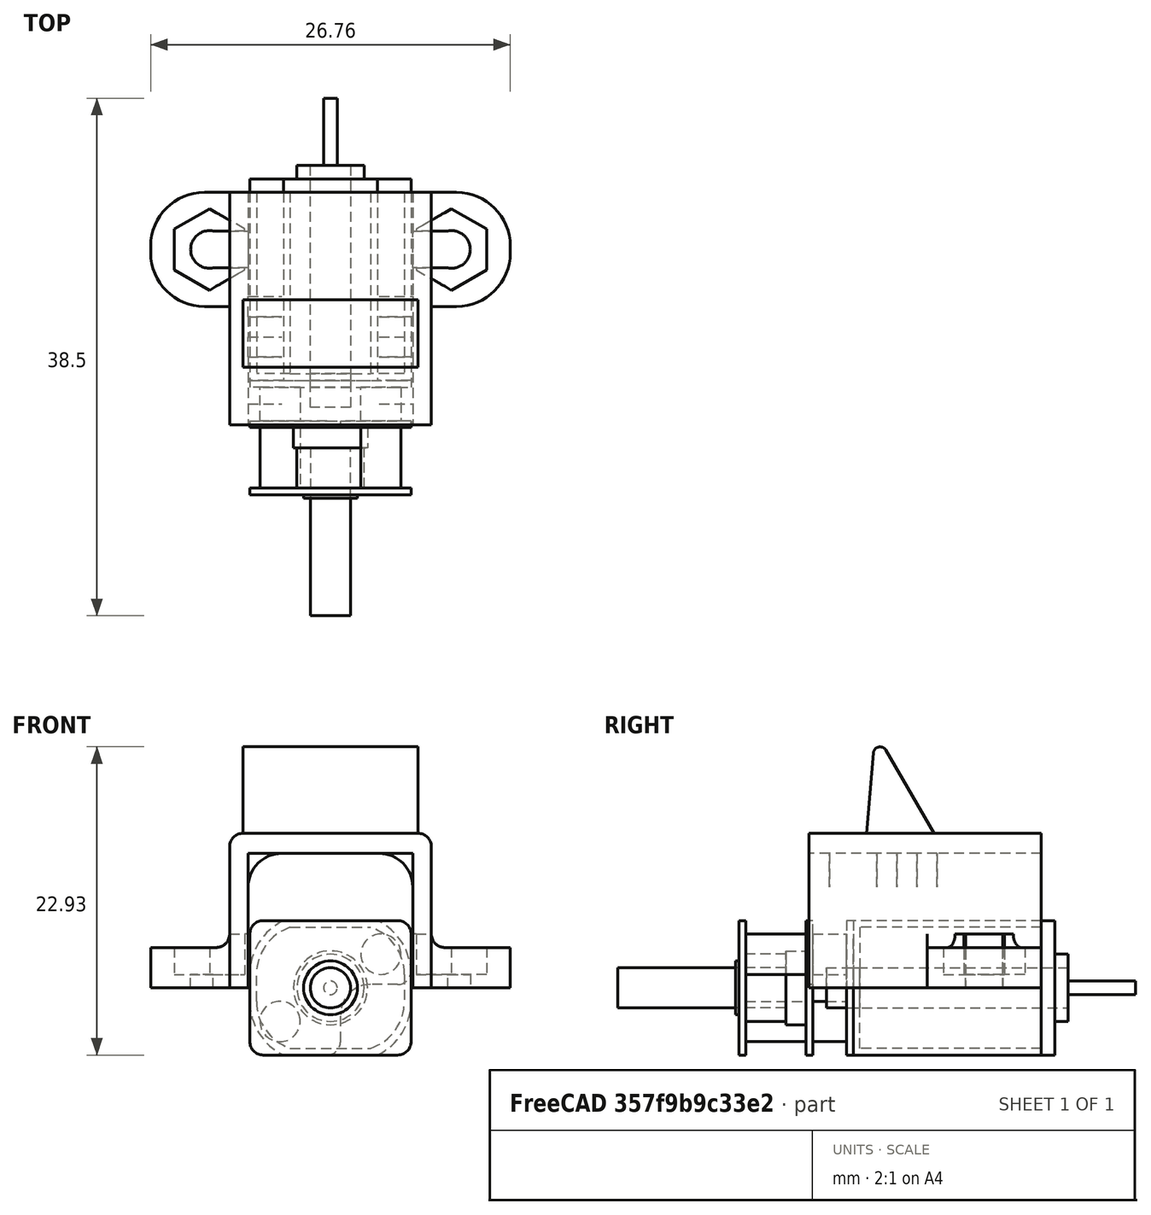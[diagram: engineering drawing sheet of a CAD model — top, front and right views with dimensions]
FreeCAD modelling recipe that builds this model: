
FCSTD DOCUMENT  (FreeCAD 0.19R24276 (Git))
Label: PB3D_MotorAndBracket
License: All rights reserved
LicenseURL: http://en.wikipedia.org/wiki/All_rights_reserved
objects: Sketcher::SketchObject×26, PartDesign::Pad×15, PartDesign::Pocket×11, PartDesign::Body×7, PartDesign::Plane×6, App::Part×2, PartDesign::Fillet×1, PartDesign::ShapeBinder×1, Mesh::Feature×1
note: 94 computed .brp shape members not serialized (recipe doc carries the construction recipe); baked Part::Feature solids carry a one-line shape summary decoded from their .brp

FEATURE [Sketcher::SketchObject] Sketch
  FullyConstrained = true
  MapMode = 5
  Placement = pos=(0,0,0) rot=(1,0,0;1.5708rad)
  Support = -> [XZ_Plane]
  sketch-geometry (12):
    g0: LineSegment StartX=-3.5 StartY=5 StartZ=0 EndX=3.5 EndY=5 EndZ=0
    g1: LineSegment StartX=-3.5 StartY=-5 StartZ=0 EndX=3.5 EndY=-5 EndZ=0
    g2: LineSegment StartX=6 StartY=1 StartZ=0 EndX=6 EndY=-1 EndZ=0
    g3: LineSegment StartX=-6 StartY=1 StartZ=0 EndX=-6 EndY=-1 EndZ=0
    g4: LineSegment StartX=0 StartY=0 StartZ=0 EndX=-6 EndY=0 EndZ=0
    g5: LineSegment StartX=0 StartY=0 StartZ=0 EndX=6 EndY=0 EndZ=0
    g6: LineSegment StartX=0 StartY=0 StartZ=0 EndX=0 EndY=5 EndZ=0
    g7: LineSegment StartX=0 StartY=0 StartZ=0 EndX=0 EndY=-5 EndZ=0
    g8: ArcOfCircle CenterX=-1.55001 CenterY=1.00001 CenterZ=0 NormalX=0 NormalY=0 NormalZ=1 AngleXU=0 Radius=4.44999 StartAngle=2.02439 EndAngle=3.14159
    g9: ArcOfCircle CenterX=1.55001 CenterY=1.00001 CenterZ=0 NormalX=0 NormalY=0 NormalZ=1 AngleXU=0 Radius=4.44999 StartAngle=6.28318 EndAngle=7.40039
    g10: ArcOfCircle CenterX=-1.55001 CenterY=-1.00001 CenterZ=0 NormalX=0 NormalY=0 NormalZ=1 AngleXU=0 Radius=4.44999 StartAngle=3.14159 EndAngle=4.25879
    g11: ArcOfCircle CenterX=1.55001 CenterY=-1.00001 CenterZ=0 NormalX=0 NormalY=0 NormalZ=1 AngleXU=0 Radius=4.44999 StartAngle=5.16598 EndAngle=6.28319
  constraints (36):
    c: Horizontal(g0)
    c: Horizontal(g1)
    c: Vertical(g2)
    c: Vertical(g3)
    c: Equal(g0,g1)
    c: Equal(g3,g2)
    c: Coincident(g4,g-1)
    c: Coincident(g5,g-1)
    c: Horizontal(g5)
    c: Coincident(g6,g-1)
    c: Coincident(g7,g-1)
    c: Vertical(g7)
    c: Vertical(g6)
    c: Horizontal(g4)
    c: Equal(g4,g5)
    c: Equal(g7,g6)
    c: Symmetric(g3,g3,g4)
    c: Symmetric(g2,g2,g5)
    c: Symmetric(g1,g1,g7)
    c: Symmetric(g0,g0,g6)
    c: Coincident(g8,g3)
    c: Coincident(g8,g0)
    c: Tangent(g8,g3)
    c: Coincident(g9,g0)
    c: Coincident(g9,g2)
    c: Coincident(g10,g3)
    c: Coincident(g10,g1)
    c: Coincident(g11,g1)
    c: Coincident(g11,g2)
    c: Tangent(g3,g10)
    c: Tangent(g9,g2)
    c: Tangent(g11,g2)
    c: DistanceY(g1,g0) = 10
    c: Distance(g2) = 2
    c: DistanceX(g3,g2) = 12
    c: DistanceX(g0,g0) = 7
FEATURE [PartDesign::Pad] Pad
  Direction = (1,1,1)
  Length = 14
  Length2 = 100
  Placement = pos=(0,0,0) rot=(1,0,0;1.5708rad)
  Profile = -> Sketch
  Type = 0
FEATURE [Sketcher::SketchObject] Sketch001
  FullyConstrained = true
  MapMode = 5
  Placement = pos=(0,0,0) rot=(1,0,0;1.5708rad)
  Support = -> [XZ_Plane]
  sketch-geometry (12):
    g0: LineSegment StartX=-3 StartY=4.5 StartZ=0 EndX=3 EndY=4.5 EndZ=0
    g1: LineSegment StartX=5.5 StartY=1 StartZ=0 EndX=5.5 EndY=-1 EndZ=0
    g2: LineSegment StartX=-3 StartY=-4.5 StartZ=0 EndX=3 EndY=-4.5 EndZ=0
    g3: LineSegment StartX=-5.5 StartY=-1 StartZ=0 EndX=-5.5 EndY=1 EndZ=0
    g4: LineSegment StartX=0 StartY=0 StartZ=0 EndX=0 EndY=4.5 EndZ=0
    g5: LineSegment StartX=0 StartY=0 StartZ=0 EndX=5.5 EndY=0 EndZ=0
    g6: LineSegment StartX=0 StartY=0 StartZ=0 EndX=0 EndY=-4.5 EndZ=0
    g7: LineSegment StartX=0 StartY=0 StartZ=0 EndX=-5.5 EndY=0 EndZ=0
    g8: ArcOfCircle CenterX=-1.79999 CenterY=0.999993 CenterZ=0 NormalX=0 NormalY=0 NormalZ=1 AngleXU=0 Radius=3.70001 StartAngle=1.9011 EndAngle=3.14159
    g9: ArcOfCircle CenterX=1.79999 CenterY=0.999993 CenterZ=0 NormalX=0 NormalY=0 NormalZ=1 AngleXU=0 Radius=3.70001 StartAngle=1.80818e-06 EndAngle=1.2405
    g10: ArcOfCircle CenterX=1.79999 CenterY=-0.999993 CenterZ=0 NormalX=0 NormalY=0 NormalZ=1 AngleXU=0 Radius=3.70001 StartAngle=5.04269 EndAngle=6.28318
    g11: ArcOfCircle CenterX=-1.79999 CenterY=-0.999993 CenterZ=0 NormalX=0 NormalY=0 NormalZ=1 AngleXU=0 Radius=3.70001 StartAngle=3.14159 EndAngle=4.38209
  constraints (36):
    c: Vertical(g3)
    c: Vertical(g1)
    c: Horizontal(g0)
    c: Horizontal(g2)
    c: Coincident(g4,g-1)
    c: Coincident(g5,g-1)
    c: Coincident(g6,g-1)
    c: Coincident(g7,g-1)
    c: Horizontal(g7)
    c: Horizontal(g5)
    c: Vertical(g4)
    c: Vertical(g6)
    c: Equal(g3,g1)
    c: Equal(g0,g2)
    c: Equal(g6,g4)
    c: Equal(g5,g7)
    c: Symmetric(g0,g0,g4)
    c: Symmetric(g1,g1,g5)
    c: Symmetric(g3,g3,g7)
    c: Symmetric(g2,g2,g6)
    c: Coincident(g8,g3)
    c: Coincident(g8,g0)
    c: Coincident(g9,g0)
    c: Coincident(g9,g1)
    c: Coincident(g10,g1)
    c: Coincident(g10,g2)
    c: Coincident(g11,g3)
    c: Coincident(g11,g2)
    c: Tangent(g8,g3)
    c: Tangent(g11,g3)
    c: Tangent(g10,g1)
    c: Tangent(g9,g1)
    c: Distance(g0) = 6
    c: Distance(g1) = 2
    c: DistanceX(g3,g1) = 11
    c: DistanceY(g2,g0) = 9
FEATURE [PartDesign::Pocket] Pocket
  BaseFeature = -> Pad
  Length = 13.5
  Length2 = 100
  Placement = pos=(0,0,0) rot=(1,0,0;1.5708rad)
  Profile = -> Sketch001
  Reversed = true
  Type = 0
FEATURE [Sketcher::SketchObject] Sketch002
  FullyConstrained = true
  MapMode = 5
  Placement = pos=(0,0,0) rot=(1,0,0;1.5708rad)
  Support = -> [XZ_Plane]
  sketch-geometry (1):
    g0: Circle CenterX=0 CenterY=0 CenterZ=0 NormalX=0 NormalY=0 NormalZ=1 AngleXU=0 Radius=1.5
  constraints (2):
    c: Coincident(g0,g-1)
    c: Diameter(g0) = 3
FEATURE [PartDesign::Pocket] Pocket001
  BaseFeature = -> Pocket
  Length = 5
  Length2 = 100
  Placement = pos=(0,0,0) rot=(1,0,0;1.5708rad)
  Profile = -> Sketch002
  Reversed = true
  Type = 1
FEATURE [PartDesign::Body] Body  label="MotorShell"
  Group = -> [Sketch,Pad,Sketch001,Pocket,Sketch002,Pocket001]
  Origin = -> Origin
  Tip = -> Pocket001
FEATURE [Sketcher::SketchObject] Sketch003
  FullyConstrained = true
  MapMode = 5
  Placement = pos=(0,0,0) rot=(1,0,0;1.5708rad)
  Support = -> [XZ_Plane002]
  sketch-geometry (12):
    g0: LineSegment StartX=-3.5 StartY=5 StartZ=0 EndX=3.5 EndY=5 EndZ=0
    g1: LineSegment StartX=6 StartY=1 StartZ=0 EndX=6 EndY=-1 EndZ=0
    g2: LineSegment StartX=3.5 StartY=-5 StartZ=0 EndX=-3.5 EndY=-5 EndZ=0
    g3: LineSegment StartX=-6 StartY=-1 StartZ=0 EndX=-6 EndY=1 EndZ=0
    g4: LineSegment StartX=0 StartY=0 StartZ=0 EndX=-6 EndY=0 EndZ=0
    g5: LineSegment StartX=0 StartY=0 StartZ=0 EndX=6 EndY=0 EndZ=0
    g6: LineSegment StartX=0 StartY=0 StartZ=0 EndX=0 EndY=5 EndZ=0
    g7: LineSegment StartX=0 StartY=0 StartZ=0 EndX=0 EndY=-5 EndZ=0
    g8: ArcOfCircle CenterX=-1.55 CenterY=1 CenterZ=0 NormalX=0 NormalY=0 NormalZ=1 AngleXU=0 Radius=4.45 StartAngle=2.02439 EndAngle=3.14159
    g9: ArcOfCircle CenterX=1.55 CenterY=1 CenterZ=0 NormalX=0 NormalY=0 NormalZ=1 AngleXU=0 Radius=4.45 StartAngle=6.28319 EndAngle=7.40038
    g10: ArcOfCircle CenterX=1.55 CenterY=-1 CenterZ=0 NormalX=0 NormalY=0 NormalZ=1 AngleXU=0 Radius=4.45 StartAngle=5.16599 EndAngle=6.28319
    g11: ArcOfCircle CenterX=-1.55 CenterY=-1 CenterZ=0 NormalX=0 NormalY=0 NormalZ=1 AngleXU=0 Radius=4.45 StartAngle=3.14159 EndAngle=4.25879
  constraints (36):
    c: Coincident(g4,g-1)
    c: PointOnObject(g4,g-1)
    c: Coincident(g5,g-1)
    c: PointOnObject(g5,g-1)
    c: Coincident(g6,g-1)
    c: PointOnObject(g6,g-2)
    c: Coincident(g7,g-1)
    c: PointOnObject(g7,g-2)
    c: Equal(g4,g5)
    c: Equal(g7,g6)
    c: Equal(g0,g2)
    c: Equal(g1,g3)
    c: Vertical(g3)
    c: Vertical(g1)
    c: Horizontal(g0)
    c: Horizontal(g2)
    c: Symmetric(g3,g3,g4)
    c: Symmetric(g1,g1,g5)
    c: Symmetric(g0,g0,g6)
    c: Symmetric(g2,g2,g7)
    c: Coincident(g8,g3)
    c: Coincident(g8,g0)
    c: Coincident(g9,g0)
    c: Coincident(g9,g1)
    c: Coincident(g10,g1)
    c: Coincident(g10,g2)
    c: Coincident(g11,g2)
    c: Coincident(g11,g3)
    c: Tangent(g8,g3)
    c: Tangent(g3,g11)
    c: Tangent(g10,g1)
    c: Tangent(g1,g9)
    c: Distance(g1) = 2
    c: Distance(g0) = 7
    c: DistanceX(g3,g1) = 12
    c: DistanceY(g2,g0) = 10
FEATURE [PartDesign::Pad] Pad001
  Direction = (1,1,1)
  Length = 1
  Length2 = 100
  Placement = pos=(0,0,0) rot=(1,0,0;1.5708rad)
  Profile = -> Sketch003
  Reversed = true
  Type = 0
FEATURE [Sketcher::SketchObject] Sketch004
  FullyConstrained = true
  MapMode = 5
  Placement = pos=(0,1,-4e-16) rot=(-1,0,0;1.5708rad)
  Support = -> [Pad001]
  sketch-geometry (1):
    g0: Circle CenterX=0 CenterY=0 CenterZ=0 NormalX=0 NormalY=0 NormalZ=1 AngleXU=0 Radius=2.5
  constraints (2):
    c: Coincident(g0,g-1)
    c: Diameter(g0) = 5
FEATURE [PartDesign::Pad] Pad002
  BaseFeature = -> Pad001
  Direction = (1,1,1)
  Length = 1
  Length2 = 100
  Placement = pos=(0,0,0) rot=(1,0,0;1.5708rad)
  Profile = -> Sketch004
  Type = 0
FEATURE [Sketcher::SketchObject] Sketch005
  FullyConstrained = true
  MapMode = 5
  Placement = pos=(0,2,-1.8e-15) rot=(-1,0,0;1.5708rad)
  Support = -> [Pad002]
  sketch-geometry (1):
    g0: Circle CenterX=0 CenterY=0 CenterZ=0 NormalX=0 NormalY=0 NormalZ=1 AngleXU=0 Radius=1.5
  constraints (2):
    c: Coincident(g0,g-1)
    c: Diameter(g0) = 3
FEATURE [PartDesign::Pocket] Pocket002
  BaseFeature = -> Pad002
  Length = 5
  Length2 = 100
  Placement = pos=(0,0,0) rot=(1,0,0;1.5708rad)
  Profile = -> Sketch005
  Type = 1
FEATURE [PartDesign::Body] Body001  label="BackPlate"
  Group = -> [Sketch003,Pad001,Sketch004,Pad002,Sketch005,Pocket002]
  Origin = -> Origin002
  Tip = -> Pocket002
FEATURE [PartDesign::Plane] DatumPlane
  AttachmentOffset = pos=(0,0,14) rot=(0,0,1;0rad)
  Length = 60
  MapMode = 2
  Placement = pos=(0,-14,-3.1e-15) rot=(1,0,0;1.5708rad)
  ResizeMode = 0
  Support = -> [XZ_Plane003]
  Width = 60
FEATURE [Sketcher::SketchObject] Sketch006
  FullyConstrained = true
  MapMode = 5
  Placement = pos=(0,-14,-3.1e-15) rot=(1,0,0;1.5708rad)
  Support = -> [DatumPlane]
  sketch-geometry (6):
    g0: LineSegment StartX=-6 StartY=5 StartZ=0 EndX=6 EndY=5 EndZ=0
    g1: LineSegment StartX=6 StartY=5 StartZ=0 EndX=6 EndY=-5 EndZ=0
    g2: LineSegment StartX=6 StartY=-5 StartZ=0 EndX=-6 EndY=-5 EndZ=0
    g3: LineSegment StartX=-6 StartY=-5 StartZ=0 EndX=-6 EndY=5 EndZ=0
    g4: LineSegment StartX=0 StartY=0 StartZ=0 EndX=0 EndY=5 EndZ=0
    g5: LineSegment StartX=0 StartY=0 StartZ=0 EndX=6 EndY=-2e-16 EndZ=0
  constraints (16):
    c: Coincident(g0,g1)
    c: Coincident(g1,g2)
    c: Coincident(g2,g3)
    c: Coincident(g3,g0)
    c: Horizontal(g0)
    c: Horizontal(g2)
    c: Vertical(g1)
    c: Vertical(g3)
    c: Coincident(g4,g-1)
    c: PointOnObject(g4,g-2)
    c: Coincident(g5,g-1)
    c: PointOnObject(g5,g-1)
    c: Symmetric(g0,g0,g4)
    c: Symmetric(g0,g1,g5)
    c: Distance(g0) = 12
    c: Distance(g1) = 10
FEATURE [PartDesign::Pad] Pad003
  Direction = (1,1,1)
  Length = 0.5
  Length2 = 100
  Placement = pos=(0,-14,3e-15) rot=(1,0,0;1.5708rad)
  Profile = -> Sketch006
  Type = 0
FEATURE [Sketcher::SketchObject] Sketch007
  FullyConstrained = true
  MapMode = 5
  Placement = pos=(0,-14.5,3.3e-15) rot=(1,0,0;1.5708rad)
  Support = -> [Pad003]
  sketch-geometry (8):
    g0: Circle CenterX=3.75 CenterY=2.5 CenterZ=0 NormalX=0 NormalY=0 NormalZ=1 AngleXU=0 Radius=1.5
    g1: Circle CenterX=-3.75 CenterY=-2.5 CenterZ=0 NormalX=0 NormalY=0 NormalZ=1 AngleXU=0 Radius=1.5
    g2: LineSegment StartX=-3.75 StartY=2.5 StartZ=0 EndX=3.75 EndY=2.5 EndZ=0
    g3: LineSegment StartX=3.75 StartY=2.5 StartZ=0 EndX=3.75 EndY=-2.5 EndZ=0
    g4: LineSegment StartX=3.75 StartY=-2.5 StartZ=0 EndX=-3.75 EndY=-2.5 EndZ=0
    g5: LineSegment StartX=-3.75 StartY=-2.5 StartZ=0 EndX=-3.75 EndY=2.5 EndZ=0
    g6: LineSegment StartX=0 StartY=0 StartZ=0 EndX=0 EndY=2.5 EndZ=0
    g7: LineSegment StartX=0 StartY=0 StartZ=0 EndX=3.75 EndY=0 EndZ=0
  constraints (20):
    c: Equal(g0,g1)
    c: Diameter(g0) = 3
    c: Coincident(g2,g3)
    c: Coincident(g3,g4)
    c: Coincident(g4,g5)
    c: Coincident(g5,g2)
    c: Horizontal(g2)
    c: Horizontal(g4)
    c: Vertical(g3)
    c: Vertical(g5)
    c: Coincident(g6,g-1)
    c: Coincident(g7,g-1)
    c: Horizontal(g7)
    c: Vertical(g6)
    c: Symmetric(g2,g2,g6)
    c: Symmetric(g2,g3,g7)
    c: Coincident(g0,g2)
    c: Coincident(g1,g4)
    c: DistanceX(g2,g0) = 7.5
    c: DistanceY(g3,g0) = 5
FEATURE [PartDesign::Pad] Pad004
  BaseFeature = -> Pad003
  Direction = (1,1,1)
  Length = 7.7
  Length2 = 100
  Placement = pos=(0,-14,3e-15) rot=(1,0,0;1.5708rad)
  Profile = -> Sketch007
  Type = 0
FEATURE [PartDesign::Plane] DatumPlane001
  AttachmentOffset = pos=(0,0,17) rot=(0,0,1;0rad)
  Length = 60
  MapMode = 5
  Placement = pos=(0,-17,-3.8e-15) rot=(1,0,0;1.5708rad)
  ResizeMode = 0
  Support = -> [XZ_Plane003]
  Width = 60
FEATURE [Sketcher::SketchObject] Sketch008
  FullyConstrained = true
  MapMode = 5
  Placement = pos=(0,-17,-3.8e-15) rot=(1,0,0;1.5708rad)
  Support = -> [DatumPlane001]
  sketch-geometry (6):
    g0: LineSegment StartX=-6 StartY=5 StartZ=0 EndX=6 EndY=5 EndZ=0
    g1: LineSegment StartX=6 StartY=5 StartZ=0 EndX=6 EndY=-5 EndZ=0
    g2: LineSegment StartX=6 StartY=-5 StartZ=0 EndX=-6 EndY=-5 EndZ=0
    g3: LineSegment StartX=-6 StartY=-5 StartZ=0 EndX=-6 EndY=5 EndZ=0
    g4: LineSegment StartX=0 StartY=0 StartZ=0 EndX=0 EndY=5 EndZ=0
    g5: LineSegment StartX=0 StartY=0 StartZ=0 EndX=6 EndY=1e-16 EndZ=0
  constraints (16):
    c: Coincident(g0,g1)
    c: Coincident(g1,g2)
    c: Coincident(g2,g3)
    c: Coincident(g3,g0)
    c: Horizontal(g0)
    c: Horizontal(g2)
    c: Vertical(g1)
    c: Vertical(g3)
    c: Coincident(g4,g-1)
    c: PointOnObject(g4,g-2)
    c: Coincident(g5,g-1)
    c: PointOnObject(g5,g-1)
    c: Symmetric(g0,g0,g4)
    c: Symmetric(g0,g1,g5)
    c: Distance(g0) = 12
    c: Distance(g1) = 10
FEATURE [PartDesign::Pad] Pad005
  BaseFeature = -> Pad004
  Direction = (1,1,1)
  Length = 0.5
  Length2 = 100
  Placement = pos=(0,-14,3e-15) rot=(1,0,0;1.5708rad)
  Profile = -> Sketch008
  Type = 0
FEATURE [PartDesign::Plane] DatumPlane002
  AttachmentOffset = pos=(0,0,22) rot=(0,0,1;0rad)
  Length = 60
  MapMode = 5
  Placement = pos=(0,-22,-4.9e-15) rot=(1,0,0;1.5708rad)
  ResizeMode = 0
  Support = -> [XZ_Plane003]
  Width = 60
FEATURE [Sketcher::SketchObject] Sketch009
  FullyConstrained = true
  MapMode = 5
  Placement = pos=(0,-22,-4.9e-15) rot=(1,0,0;1.5708rad)
  Support = -> [DatumPlane002]
  sketch-geometry (6):
    g0: LineSegment StartX=0 StartY=0 StartZ=0 EndX=0 EndY=5 EndZ=0
    g1: LineSegment StartX=0 StartY=0 StartZ=0 EndX=6 EndY=0 EndZ=0
    g2: LineSegment StartX=-6 StartY=5 StartZ=0 EndX=6 EndY=5 EndZ=0
    g3: LineSegment StartX=6 StartY=5 StartZ=0 EndX=6 EndY=-5 EndZ=0
    g4: LineSegment StartX=6 StartY=-5 StartZ=0 EndX=-6 EndY=-5 EndZ=0
    g5: LineSegment StartX=-6 StartY=-5 StartZ=0 EndX=-6 EndY=5 EndZ=0
  constraints (16):
    c: Coincident(g0,g-1)
    c: Coincident(g1,g-1)
    c: Horizontal(g1)
    c: Vertical(g0)
    c: Coincident(g2,g3)
    c: Coincident(g3,g4)
    c: Coincident(g4,g5)
    c: Coincident(g5,g2)
    c: Horizontal(g2)
    c: Horizontal(g4)
    c: Vertical(g3)
    c: Vertical(g5)
    c: Symmetric(g2,g2,g0)
    c: Symmetric(g2,g3,g1)
    c: Distance(g2) = 12
    c: Distance(g3) = 10
FEATURE [PartDesign::Pad] Pad006
  BaseFeature = -> Pad005
  Direction = (1,1,1)
  Length = 0.5
  Length2 = 100
  Placement = pos=(0,-14,3e-15) rot=(1,0,0;1.5708rad)
  Profile = -> Sketch009
  Type = 0
FEATURE [Sketcher::SketchObject] Sketch010
  FullyConstrained = true
  MapMode = 5
  Placement = pos=(0,-22.5,4.9e-15) rot=(1,0,0;1.5708rad)
  Support = -> [Pad006]
  sketch-geometry (1):
    g0: Circle CenterX=0 CenterY=0 CenterZ=0 NormalX=0 NormalY=0 NormalZ=1 AngleXU=0 Radius=2
  constraints (2):
    c: Coincident(g0,g-1)
    c: Diameter(g0) = 4
FEATURE [PartDesign::Pad] Pad007
  BaseFeature = -> Pad006
  Direction = (1,1,1)
  Length = 0.25
  Length2 = 100
  Placement = pos=(0,-14,3e-15) rot=(1,0,0;1.5708rad)
  Profile = -> Sketch010
  Type = 0
FEATURE [Sketcher::SketchObject] Sketch011
  FullyConstrained = true
  MapMode = 5
  Placement = pos=(0,-22,4.8e-15) rot=(-1,0,0;1.5708rad)
  Support = -> [Pad007]
  sketch-geometry (1):
    g0: Circle CenterX=0 CenterY=0 CenterZ=0 NormalX=0 NormalY=0 NormalZ=1 AngleXU=0 Radius=2.5
  constraints (2):
    c: Coincident(g0,g-1)
    c: Diameter(g0) = 5
FEATURE [PartDesign::Pad] Pad008
  BaseFeature = -> Pad007
  Direction = (1,1,1)
  Length = 3
  Length2 = 100
  Placement = pos=(0,-14,3e-15) rot=(1,0,0;1.5708rad)
  Profile = -> Sketch011
  Type = 0
FEATURE [Sketcher::SketchObject] Sketch012
  FullyConstrained = true
  MapMode = 5
  Placement = pos=(0,-22.75,4.9e-15) rot=(1,0,0;1.5708rad)
  Support = -> [Pad008]
  sketch-geometry (1):
    g0: Circle CenterX=0 CenterY=0 CenterZ=0 NormalX=0 NormalY=0 NormalZ=1 AngleXU=0 Radius=1.5
  constraints (2):
    c: Coincident(g0,g-1)
    c: Diameter(g0) = 3
FEATURE [PartDesign::Pocket] Pocket003
  BaseFeature = -> Pad008
  Length = 5
  Length2 = 100
  Placement = pos=(0,-14,3e-15) rot=(1,0,0;1.5708rad)
  Profile = -> Sketch012
  Type = 0
FEATURE [Sketcher::SketchObject] Sketch013
  FullyConstrained = true
  MapMode = 5
  Placement = pos=(0,-17.5,3.8e-15) rot=(1,0,0;1.5708rad)
  Support = -> [Pocket003]
  sketch-geometry (5):
    g0: LineSegment StartX=7.00002 StartY=0.25 StartZ=0 EndX=7.00002 EndY=-6 EndZ=0
    g1: LineSegment StartX=7.00002 StartY=-6 StartZ=0 EndX=0.75 EndY=-6 EndZ=0
    g2: LineSegment StartX=0.75 StartY=-2 StartZ=0 EndX=0.75 EndY=-6 EndZ=0
    g3: LineSegment StartX=3.00002 StartY=0.25 StartZ=0 EndX=7.00002 EndY=0.25 EndZ=0
    g4: ArcOfCircle CenterX=3 CenterY=-2 CenterZ=0 NormalX=0 NormalY=0 NormalZ=1 AngleXU=0 Radius=2.25 StartAngle=1.57079 EndAngle=3.14159
  constraints (16):
    c: Coincident(g0,g1)
    c: Horizontal(g1)
    c: Vertical(g0)
    c: Coincident(g2,g1)
    c: Vertical(g2)
    c: Coincident(g3,g0)
    c: Horizontal(g3)
    c: Coincident(g4,g3)
    c: DistanceX(g-1,g4) = 3
    c: DistanceY(g4,g-1) = 2
    c: Coincident(g4,g2)
    c: Diameter(g4) = 4.5
    c: Equal(g3,g2)
    c: Tangent(g4,g3)
    c: Tangent(g4,g2)
    c: Distance(g3) = 4
FEATURE [PartDesign::Pocket] Pocket004
  BaseFeature = -> Pocket003
  Length = 1
  Length2 = 100
  Placement = pos=(0,-14,3e-15) rot=(1,0,0;1.5708rad)
  Profile = -> Sketch013
  Type = 0
FEATURE [PartDesign::Fillet] Fillet
  Base = -> Pocket004 [Edge52,Edge38,Edge2,Edge51,Edge27,Edge1,Edge54,Edge26,Edge5,Edge56,Edge8,Edge36,Edge30]
  BaseFeature = -> Pocket004
  Placement = pos=(0,-14,3e-15) rot=(1,0,0;1.5708rad)
  Radius = 1
  SupportTransform = false
FEATURE [Sketcher::SketchObject] Sketch014
  FullyConstrained = true
  MapMode = 5
  Placement = pos=(0,-14,3e-15) rot=(-1,0,0;1.5708rad)
  Support = -> [Fillet]
  sketch-geometry (1):
    g0: Circle CenterX=0 CenterY=0 CenterZ=0 NormalX=0 NormalY=0 NormalZ=1 AngleXU=0 Radius=1.5
  constraints (2):
    c: Coincident(g0,g-1)
    c: Diameter(g0) = 3
FEATURE [PartDesign::Pocket] Pocket005
  BaseFeature = -> Fillet
  Length = 2
  Length2 = 100
  Placement = pos=(0,-14,3e-15) rot=(1,0,0;1.5708rad)
  Profile = -> Sketch014
  Type = 0
FEATURE [PartDesign::Body] Body002  label="GearPlates"
  Group = -> [DatumPlane,Sketch006,Pad003,Sketch007,Pad004,DatumPlane001,Sketch008,Pad005,DatumPlane002,Sketch009,Pad006,Sketch010,Pad007,Sketch011,Pad008,Sketch012,Pocket003,Sketch013,Pocket004,Fillet,Sketch014,Pocket005]
  Origin = -> Origin003
  Tip = -> Pocket005
FEATURE [PartDesign::Plane] DatumPlane003
  AttachmentOffset = pos=(0,0,-2) rot=(0,0,1;0rad)
  Length = 60
  MapMode = 5
  Placement = pos=(0,2,4e-16) rot=(1,0,0;1.5708rad)
  ResizeMode = 0
  Support = -> [XZ_Plane004]
  Width = 60
FEATURE [Sketcher::SketchObject] Sketch015
  FullyConstrained = true
  MapMode = 5
  Placement = pos=(0,2,4e-16) rot=(1,0,0;1.5708rad)
  Support = -> [DatumPlane003]
  sketch-geometry (1):
    g0: Circle CenterX=0 CenterY=0 CenterZ=0 NormalX=0 NormalY=0 NormalZ=1 AngleXU=0 Radius=1.5
  constraints (2):
    c: Coincident(g0,g-1)
    c: Diameter(g0) = 3
FEATURE [PartDesign::Pad] Pad009
  Direction = (1,1,1)
  Length = 18
  Length2 = 100
  Placement = pos=(0,2,0) rot=(1,0,0;1.5708rad)
  Profile = -> Sketch015
  Type = 0
FEATURE [PartDesign::Body] Body003  label="MotorShaft"
  Group = -> [DatumPlane003,Sketch015,Pad009]
  Origin = -> Origin004
  Tip = -> Pad009
FEATURE [PartDesign::Plane] DatumPlane004
  AttachmentOffset = pos=(0,0,17.5) rot=(0,0,1;0rad)
  Length = 60
  MapMode = 5
  Placement = pos=(0,-17.5,-3.9e-15) rot=(1,0,0;1.5708rad)
  ResizeMode = 0
  Support = -> [XZ_Plane005]
  Width = 60
FEATURE [Sketcher::SketchObject] Sketch016
  FullyConstrained = true
  MapMode = 5
  Placement = pos=(0,-17.5,-3.9e-15) rot=(1,0,0;1.5708rad)
  Support = -> [DatumPlane004]
  sketch-geometry (1):
    g0: Circle CenterX=0 CenterY=0 CenterZ=0 NormalX=0 NormalY=0 NormalZ=1 AngleXU=0 Radius=1.5
  constraints (2):
    c: Coincident(g0,g-1)
    c: Diameter(g0) = 3
FEATURE [PartDesign::Pad] Pad010
  Direction = (1,1,1)
  Length = 14
  Length2 = 100
  Placement = pos=(0,-17.5,4e-15) rot=(1,0,0;1.5708rad)
  Profile = -> Sketch016
  Type = 0
FEATURE [Sketcher::SketchObject] Sketch017
  FullyConstrained = true
  MapMode = 5
  Placement = pos=(0,-17.5,-3.9e-15) rot=(1,0,0;1.5708rad)
  Support = -> [DatumPlane004]
  sketch-geometry (1):
    g0: Circle CenterX=0 CenterY=0 CenterZ=0 NormalX=0 NormalY=0 NormalZ=1 AngleXU=0 Radius=2.75
  constraints (2):
    c: Coincident(g0,g-1)
    c: Diameter(g0) = 5.5
FEATURE [PartDesign::Pad] Pad011
  BaseFeature = -> Pad010
  Direction = (1,1,1)
  Length = 1.5
  Length2 = 100
  Placement = pos=(0,-17.5,4e-15) rot=(1,0,0;1.5708rad)
  Profile = -> Sketch017
  Type = 0
FEATURE [PartDesign::Body] Body004  label="WheelShaft"
  Group = -> [DatumPlane004,Sketch016,Pad010,Sketch017,Pad011]
  Origin = -> Origin005
  Tip = -> Pad011
FEATURE [PartDesign::ShapeBinder] CopyPad009
  TraceSupport = false
FEATURE [Sketcher::SketchObject] Sketch021
  FullyConstrained = true
  MapMode = 5
  Placement = pos=(1e-16,2,-5e-16) rot=(0,0.707107,0.707107;3.14159rad)
  Support = -> [CopyPad009]
  sketch-geometry (1):
    g0: Circle CenterX=0 CenterY=0 CenterZ=0 NormalX=0 NormalY=0 NormalZ=1 AngleXU=0 Radius=0.5
  constraints (2):
    c: Coincident(g0,g-1)
    c: Diameter(g0) = 1
FEATURE [PartDesign::Pad] Pad014
  Direction = (1,1,1)
  Length = 5
  Length2 = 100
  Profile = -> Sketch021
  Type = 0
FEATURE [PartDesign::Body] Body006  label="ExtendedBackShaft"
  Group = -> [CopyPad009,Sketch021,Pad014]
  Origin = -> Origin007
  Tip = -> Pad014
FEATURE [App::Part] Part  label="Std_MotorAssembly"
  Group = -> [Body,Body001,Body002,Body003,Body004,Body006]
  Origin = -> Origin001
FEATURE [PartDesign::Plane] DatumPlane005  label="Datum_HexSunkFeet"
  AttachmentOffset = pos=(0,0,3) rot=(0,0,1;0rad)
  Length = 60
  MapMode = 5
  Placement = pos=(0,0,3) rot=(0,0,1;0rad)
  ResizeMode = 0
  Support = -> [XY_Plane009]
  Width = 60
FEATURE [Sketcher::SketchObject] Sketch022
  FullyConstrained = true
  MapMode = 5
  Support = -> [XY_Plane009]
  sketch-geometry (4):
    g0: Circle CenterX=-9 CenterY=-4.25 CenterZ=0 NormalX=0 NormalY=0 NormalZ=1 AngleXU=0 Radius=1.4
    g1: Circle CenterX=9 CenterY=-4.25 CenterZ=0 NormalX=0 NormalY=0 NormalZ=1 AngleXU=0 Radius=1.4
    g2: LineSegment StartX=-9 StartY=-4.25 StartZ=0 EndX=9 EndY=-4.25 EndZ=0
    g3: LineSegment StartX=0 StartY=0 StartZ=0 EndX=0 EndY=-4.25 EndZ=0
  constraints (10):
    c: Coincident(g2,g0)
    c: Coincident(g2,g1)
    c: Horizontal(g2)
    c: Coincident(g3,g-1)
    c: PointOnObject(g3,g-2)
    c: Symmetric(g0,g1,g3)
    c: Equal(g0,g1)
    c: Diameter(g0) = 2.8
    c: DistanceX(g0,g1) = 18
    c: DistanceY(g3,g-1) = 4.25
FEATURE [Sketcher::SketchObject] Sketch023
  FullyConstrained = true
  MapMode = 5
  Support = -> [XY_Plane009]
  sketch-geometry (22):
    g0: LineSegment StartX=-9.375 StartY=0 StartZ=0 EndX=9.375 EndY=0 EndZ=0
    g1: LineSegment StartX=13.375 StartY=-4 StartZ=0 EndX=13.375 EndY=-4.5 EndZ=0
    g2: LineSegment StartX=9.375 StartY=-8.5 StartZ=0 EndX=7.5 EndY=-8.5 EndZ=0
    g3: LineSegment StartX=7.5 StartY=-8.5 StartZ=0 EndX=7.5 EndY=-29 EndZ=0
    g4: LineSegment StartX=7.5 StartY=-29 StartZ=0 EndX=15 EndY=-29 EndZ=0
    g5: LineSegment StartX=15 StartY=-29 StartZ=0 EndX=15 EndY=1 EndZ=0
    g6: LineSegment StartX=15 StartY=1 StartZ=0 EndX=-15 EndY=1 EndZ=0
    g7: LineSegment StartX=-15 StartY=1 StartZ=0 EndX=-15 EndY=-29 EndZ=0
    g8: LineSegment StartX=-15 StartY=-29 StartZ=0 EndX=-7.5 EndY=-29 EndZ=0
    g9: LineSegment StartX=-7.5 StartY=-29 StartZ=0 EndX=-7.5 EndY=-8.5 EndZ=0
    g10: LineSegment StartX=-7.5 StartY=-8.5 StartZ=0 EndX=-9.375 EndY=-8.5 EndZ=0
    g11: LineSegment StartX=-13.375 StartY=-4.5 StartZ=0 EndX=-13.375 EndY=-4 EndZ=0
    g12: LineSegment StartX=-7.5 StartY=-8.5 StartZ=0 EndX=7.5 EndY=-8.5 EndZ=0
    g13: LineSegment StartX=-7.5 StartY=-29 StartZ=0 EndX=7.5 EndY=-29 EndZ=0
    g14: LineSegment StartX=0 StartY=0 StartZ=0 EndX=0 EndY=1 EndZ=0
    g15: ArcOfCircle CenterX=-9.375 CenterY=-4 CenterZ=0 NormalX=0 NormalY=0 NormalZ=1 AngleXU=0 Radius=4 StartAngle=1.5708 EndAngle=3.14159
    g16: ArcOfCircle CenterX=-9.375 CenterY=-4.5 CenterZ=0 NormalX=0 NormalY=0 NormalZ=1 AngleXU=0 Radius=4 StartAngle=3.14159 EndAngle=4.71239
    g17: ArcOfCircle CenterX=9.375 CenterY=-4.5 CenterZ=0 NormalX=0 NormalY=0 NormalZ=1 AngleXU=0 Radius=4 StartAngle=4.71239 EndAngle=6.28319
    g18: ArcOfCircle CenterX=9.375 CenterY=-4 CenterZ=0 NormalX=0 NormalY=0 NormalZ=1 AngleXU=0 Radius=4 StartAngle=0 EndAngle=1.5708
    g19: LineSegment StartX=-9.375 StartY=-4 StartZ=0 EndX=9.375 EndY=-4 EndZ=0
    g20: LineSegment StartX=9.375 StartY=-4 StartZ=0 EndX=9.375 EndY=-4.5 EndZ=0
    g21: LineSegment StartX=9.375 StartY=-4.5 StartZ=0 EndX=-9.375 EndY=-4.5 EndZ=0
  constraints (55):
    c: Horizontal(g0)
    c: Vertical(g1)
    c: Horizontal(g2)
    c: Coincident(g3,g2)
    c: Vertical(g3)
    c: Coincident(g4,g3)
    c: Horizontal(g4)
    c: Coincident(g5,g4)
    c: Vertical(g5)
    c: Coincident(g6,g5)
    c: Horizontal(g6)
    c: Coincident(g7,g6)
    c: Vertical(g7)
    c: Coincident(g8,g7)
    c: Horizontal(g8)
    c: Coincident(g9,g8)
    c: Vertical(g9)
    c: Coincident(g10,g9)
    c: Horizontal(g10)
    c: Vertical(g11)
    c: Coincident(g12,g9)
    c: Coincident(g12,g2)
    c: Coincident(g13,g8)
    c: Coincident(g13,g3)
    c: Horizontal(g13)
    c: Horizontal(g12)
    c: Equal(g10,g2)
    c: PointOnObject(g14,g-2)
    c: Symmetric(g6,g5,g14)
    c: Tangent(g11,g15) = 1.5708
    c: Tangent(g0,g15) = 1.5708
    c: Tangent(g11,g16) = 1.5708
    c: Tangent(g10,g16) = 1.5708
    c: Tangent(g2,g17) = 1.5708
    c: Tangent(g1,g17) = 1.5708
    c: Tangent(g0,g18) = 1.5708
    c: Tangent(g1,g18) = 1.5708
    c: Coincident(g19,g15)
    c: Coincident(g19,g18)
    c: Horizontal(g19)
    c: Coincident(g20,g18)
    c: Coincident(g20,g17)
    c: Coincident(g21,g17)
    c: Coincident(g21,g16)
    c: Horizontal(g21)
    c: Vertical(g20)
    c: Distance(g5) = 30
    c: Symmetric(g0,g0,g-1)
    c: Radius(g18) = 4
    c: Coincident(g14,g-1)
    c: DistanceY(g-1,g5) = 1
    c: DistanceX(g8,g3) = 15
    c: DistanceX(g7,g4) = 30
    c: DistanceX(g11,g1) = 26.75
    c: DistanceY(g2,g0) = 8.5
FEATURE [Sketcher::SketchObject] Sketch024
  FullyConstrained = true
  MapMode = 5
  Placement = pos=(0,0,0) rot=(1,0,0;1.5708rad)
  Support = -> [XZ_Plane009]
  sketch-geometry (25):
    g0: LineSegment StartX=-13.5 StartY=0 StartZ=0 EndX=-6.125 EndY=0 EndZ=0
    g1: LineSegment StartX=-6.125 StartY=0 StartZ=0 EndX=-6.125 EndY=7.5 EndZ=0
    g2: LineSegment StartX=-3.625 StartY=10 StartZ=0 EndX=3.625 EndY=10 EndZ=0
    g3: LineSegment StartX=6.125 StartY=7.5 StartZ=0 EndX=6.125 EndY=0 EndZ=0
    g4: LineSegment StartX=6.125 StartY=0 StartZ=0 EndX=13.5 EndY=0 EndZ=0
    g5: LineSegment StartX=13.5 StartY=0 StartZ=0 EndX=13.5 EndY=3 EndZ=0
    g6: LineSegment StartX=13.5 StartY=3 StartZ=0 EndX=8.5 EndY=3 EndZ=0
    g7: LineSegment StartX=7.5 StartY=4 StartZ=0 EndX=7.5 EndY=10.5 EndZ=0
    g8: LineSegment StartX=6.5 StartY=11.5 StartZ=0 EndX=-6.5 EndY=11.5 EndZ=0
    g9: LineSegment StartX=-7.5 StartY=10.5 StartZ=0 EndX=-7.5 EndY=4 EndZ=0
    g10: LineSegment StartX=-8.5 StartY=3 StartZ=0 EndX=-13.5 EndY=3 EndZ=0
    g11: LineSegment StartX=-13.5 StartY=3 StartZ=0 EndX=-13.5 EndY=0 EndZ=0
    g12: LineSegment StartX=-6.125 StartY=0 StartZ=0 EndX=6.125 EndY=0 EndZ=0
    g13: LineSegment StartX=0 StartY=0 StartZ=0 EndX=0 EndY=10 EndZ=0
    g14: LineSegment StartX=0 StartY=10 StartZ=0 EndX=0 EndY=11.5 EndZ=0
    g15: ArcOfCircle CenterX=-6.5 CenterY=10.5 CenterZ=0 NormalX=0 NormalY=0 NormalZ=1 AngleXU=0 Radius=1 StartAngle=1.5708 EndAngle=3.14159
    g16: ArcOfCircle CenterX=6.5 CenterY=10.5 CenterZ=0 NormalX=0 NormalY=0 NormalZ=1 AngleXU=0 Radius=1 StartAngle=0 EndAngle=1.5708
    g17: ArcOfCircle CenterX=3.625 CenterY=7.5 CenterZ=0 NormalX=0 NormalY=0 NormalZ=1 AngleXU=0 Radius=2.5 StartAngle=0 EndAngle=1.5708
    g18: ArcOfCircle CenterX=-3.625 CenterY=7.5 CenterZ=0 NormalX=0 NormalY=0 NormalZ=1 AngleXU=0 Radius=2.5 StartAngle=1.5708 EndAngle=3.14159
    g19: ArcOfCircle CenterX=-8.5 CenterY=4 CenterZ=0 NormalX=0 NormalY=0 NormalZ=1 AngleXU=0 Radius=1 StartAngle=4.71239 EndAngle=6.28319
    g20: ArcOfCircle CenterX=8.5 CenterY=4 CenterZ=0 NormalX=0 NormalY=0 NormalZ=1 AngleXU=0 Radius=1 StartAngle=3.14159 EndAngle=4.71239
    g21: LineSegment StartX=-6.5 StartY=10.5 StartZ=0 EndX=6.5 EndY=10.5 EndZ=0
    g22: LineSegment StartX=-8.5 StartY=4 StartZ=0 EndX=8.5 EndY=4 EndZ=0
    g23: LineSegment StartX=-3.625 StartY=7.5 StartZ=0 EndX=3.625 EndY=7.5 EndZ=0
    g24: LineSegment StartX=-8.5 StartY=3 StartZ=0 EndX=8.5 EndY=3 EndZ=0
  constraints (62):
    c: Horizontal(g0)
    c: Coincident(g1,g0)
    c: Vertical(g1)
    c: Horizontal(g2)
    c: Vertical(g3)
    c: Coincident(g4,g3)
    c: Horizontal(g4)
    c: Coincident(g5,g4)
    c: Vertical(g5)
    c: Coincident(g6,g5)
    c: Horizontal(g6)
    c: Vertical(g7)
    c: Horizontal(g8)
    c: Vertical(g9)
    c: Horizontal(g10)
    c: Coincident(g11,g10)
    c: Coincident(g11,g0)
    c: Vertical(g11)
    c: Coincident(g12,g0)
    c: Coincident(g12,g3)
    c: Horizontal(g12)
    c: Coincident(g13,g-1)
    c: PointOnObject(g13,g-2)
    c: Coincident(g14,g13)
    c: PointOnObject(g14,g-2)
    c: Tangent(g9,g15) = -1.5708
    c: Tangent(g8,g15) = -1.5708
    c: Tangent(g8,g16) = -1.5708
    c: Tangent(g7,g16) = -1.5708
    c: Tangent(g2,g17) = 1.5708
    c: Tangent(g3,g17) = 1.5708
    c: Tangent(g2,g18) = 1.5708
    c: Tangent(g1,g18) = 1.5708
    c: Tangent(g9,g19) = 1.5708
    c: Tangent(g10,g19) = 1.5708
    c: Tangent(g7,g20) = 1.5708
    c: Tangent(g6,g20) = 1.5708
    c: Coincident(g21,g15)
    c: Coincident(g21,g16)
    c: Horizontal(g21)
    c: Coincident(g22,g19)
    c: Coincident(g22,g20)
    c: Horizontal(g22)
    c: Coincident(g23,g18)
    c: Coincident(g23,g17)
    c: Horizontal(g23)
    c: Symmetric(g8,g8,g14)
    c: Symmetric(g2,g2,g13)
    c: Equal(g0,g4)
    c: PointOnObject(g0,g-1)
    c: Distance(g12) = 12.25
    c: Radius(g15) = 1
    c: Radius(g19) = 1
    c: Coincident(g24,g10)
    c: Coincident(g24,g6)
    c: Horizontal(g24)
    c: DistanceX(g9,g7) = 15
    c: DistanceY(g4,g8) = 11.5
    c: DistanceY(g-1,g2) = 10
    c: DistanceY(g-1,g5) = 3
    c: DistanceX(g0,g4) = 27
    c: Radius(g18) = 2.5
FEATURE [Sketcher::SketchObject] Sketch025
  FullyConstrained = true
  MapMode = 5
  Placement = pos=(0,0,3) rot=(0,0,1;0rad)
  Support = -> [DatumPlane005]
  sketch-geometry (16):
    g0: LineSegment StartX=-6.375 StartY=-5.76554 StartZ=0 EndX=-6.375 EndY=-2.73446 EndZ=0
    g1: LineSegment StartX=-6.375 StartY=-2.73446 StartZ=0 EndX=-9 EndY=-1.21891 EndZ=0
    g2: LineSegment StartX=-9 StartY=-1.21891 StartZ=0 EndX=-11.625 EndY=-2.73446 EndZ=0
    g3: LineSegment StartX=-11.625 StartY=-2.73446 StartZ=0 EndX=-11.625 EndY=-5.76554 EndZ=0
    g4: LineSegment StartX=-11.625 StartY=-5.76554 StartZ=0 EndX=-9 EndY=-7.28109 EndZ=0
    g5: LineSegment StartX=-9 StartY=-7.28109 StartZ=0 EndX=-6.375 EndY=-5.76554 EndZ=0
    g6: Circle CenterX=-9 CenterY=-4.25 CenterZ=0 NormalX=0 NormalY=0 NormalZ=1 AngleXU=0 Radius=3.03109
    g7: LineSegment StartX=11.625 StartY=-5.76554 StartZ=0 EndX=11.625 EndY=-2.73446 EndZ=0
    g8: LineSegment StartX=11.625 StartY=-2.73446 StartZ=0 EndX=9 EndY=-1.21891 EndZ=0
    g9: LineSegment StartX=9 StartY=-1.21891 StartZ=0 EndX=6.375 EndY=-2.73446 EndZ=0
    g10: LineSegment StartX=6.375 StartY=-2.73446 StartZ=0 EndX=6.375 EndY=-5.76554 EndZ=0
    g11: LineSegment StartX=6.375 StartY=-5.76554 StartZ=0 EndX=9 EndY=-7.28109 EndZ=0
    g12: LineSegment StartX=9 StartY=-7.28109 StartZ=0 EndX=11.625 EndY=-5.76554 EndZ=0
    g13: Circle CenterX=9 CenterY=-4.25 CenterZ=0 NormalX=0 NormalY=0 NormalZ=1 AngleXU=0 Radius=3.03109
    g14: LineSegment StartX=-9 StartY=-4.25 StartZ=0 EndX=9 EndY=-4.25 EndZ=0
    g15: LineSegment StartX=0 StartY=0 StartZ=0 EndX=0 EndY=-4.25 EndZ=0
  constraints (38):
    c: Coincident(g0,g1)
    c: Coincident(g1,g2)
    c: Coincident(g2,g3)
    c: Coincident(g3,g4)
    c: Coincident(g4,g5)
    c: Coincident(g5,g0)
    c: Equal(g0, g1-g5) x5
    c: PointOnObject(g0,g6)
    c: PointOnObject(g1,g6)
    c: PointOnObject(g2,g6)
    c: PointOnObject(g3,g6)
    c: PointOnObject(g4,g6)
    c: PointOnObject(g5,g6)
    c: Coincident(g7,g8)
    c: Coincident(g8,g9)
    c: Coincident(g9,g10)
    c: Coincident(g10,g11)
    c: Coincident(g11,g12)
    c: Coincident(g12,g7)
    c: Equal(g7, g8-g12) x5
    c: PointOnObject(g7,g13)
    c: PointOnObject(g8,g13)
    c: PointOnObject(g9,g13)
    c: PointOnObject(g10,g13)
    c: PointOnObject(g11,g13)
    c: PointOnObject(g12,g13)
    c: Vertical(g3)
    c: Vertical(g10)
    c: Equal(g6,g13)
    c: Coincident(g14,g6)
    c: Coincident(g14,g13)
    c: Horizontal(g14)
    c: Coincident(g15,g-1)
    c: PointOnObject(g15,g-2)
    c: Symmetric(g6,g13,g15)
    c: DistanceX(g6,g13) = 18
    c: Distance(g15) = 4.25
    c: DistanceX(g2,g0) = 5.25
FEATURE [Sketcher::SketchObject] Sketch026
  FullyConstrained = true
  MapMode = 5
  Support = -> [XY_Plane009]
  sketch-geometry (7):
    g0: LineSegment StartX=-9 StartY=-2.875 StartZ=0 EndX=9 EndY=-2.875 EndZ=0
    g1: LineSegment StartX=9 StartY=-2.875 StartZ=0 EndX=9 EndY=-5.625 EndZ=0
    g2: LineSegment StartX=9 StartY=-5.625 StartZ=0 EndX=-9 EndY=-5.625 EndZ=0
    g3: LineSegment StartX=-9 StartY=-5.625 StartZ=0 EndX=-9 EndY=-2.875 EndZ=0
    g4: LineSegment StartX=-9 StartY=-4.25 StartZ=0 EndX=9 EndY=-4.25 EndZ=0
    g5: GeomPoint X=-9e-16 Y=-4.25 Z=0
    g6: LineSegment StartX=0 StartY=0 StartZ=0 EndX=0 EndY=-4.25 EndZ=0
  constraints (17):
    c: Coincident(g0,g1)
    c: Coincident(g1,g2)
    c: Coincident(g2,g3)
    c: Coincident(g3,g0)
    c: Horizontal(g0)
    c: Horizontal(g2)
    c: Vertical(g1)
    c: Vertical(g3)
    c: Distance(g1) = 2.75
    c: Symmetric(g2,g0,g4)
    c: Symmetric(g0,g1,g4)
    c: Symmetric(g4,g4,g5)
    c: Coincident(g6,g-1)
    c: PointOnObject(g6,g-2)
    c: Symmetric(g4,g4,g6)
    c: DistanceX(g2,g1) = 18
    c: Distance(g6) = 4.25
FEATURE [Sketcher::SketchObject] Sketch027
  FullyConstrained = true
  MapMode = 5
  Support = -> [XY_Plane009]
  sketch-geometry (17):
    g0: LineSegment StartX=-6.125 StartY=-7.75 StartZ=0 EndX=6.125 EndY=-7.75 EndZ=0
    g1: LineSegment StartX=6.125 StartY=-7.75 StartZ=0 EndX=6.125 EndY=-9.25 EndZ=0
    g2: LineSegment StartX=6.125 StartY=-9.25 StartZ=0 EndX=-6.125 EndY=-9.25 EndZ=0
    g3: LineSegment StartX=-6.125 StartY=-9.25 StartZ=0 EndX=-6.125 EndY=-7.75 EndZ=0
    g4: LineSegment StartX=-6.125 StartY=-10.75 StartZ=0 EndX=6.125 EndY=-10.75 EndZ=0
    g5: LineSegment StartX=6.125 StartY=-10.75 StartZ=0 EndX=6.125 EndY=-12.25 EndZ=0
    g6: LineSegment StartX=6.125 StartY=-12.25 StartZ=0 EndX=-6.125 EndY=-12.25 EndZ=0
    g7: LineSegment StartX=-6.125 StartY=-12.25 StartZ=0 EndX=-6.125 EndY=-10.75 EndZ=0
    g8: LineSegment StartX=-6.125 StartY=-15.75 StartZ=0 EndX=6.125 EndY=-15.75 EndZ=0
    g9: LineSegment StartX=6.125 StartY=-15.75 StartZ=0 EndX=6.125 EndY=-17.75 EndZ=0
    g10: LineSegment StartX=6.125 StartY=-17.75 StartZ=0 EndX=-6.125 EndY=-17.75 EndZ=0
    g11: LineSegment StartX=-6.125 StartY=-17.75 StartZ=0 EndX=-6.125 EndY=-15.75 EndZ=0
    g12: LineSegment StartX=-6.125 StartY=-9.25 StartZ=0 EndX=-6.125 EndY=-10.75 EndZ=0
    g13: LineSegment StartX=-6.125 StartY=-12.25 StartZ=0 EndX=-6.125 EndY=-15.75 EndZ=0
    g14: LineSegment StartX=6.125 StartY=-9.25 StartZ=0 EndX=6.125 EndY=-10.75 EndZ=0
    g15: LineSegment StartX=6.125 StartY=-12.25 StartZ=0 EndX=6.125 EndY=-15.75 EndZ=0
    g16: LineSegment StartX=0 StartY=0 StartZ=0 EndX=0 EndY=-7.75 EndZ=0
  constraints (46):
    c: Coincident(g0,g1)
    c: Coincident(g1,g2)
    c: Coincident(g2,g3)
    c: Coincident(g3,g0)
    c: Horizontal(g0)
    c: Horizontal(g2)
    c: Vertical(g1)
    c: Vertical(g3)
    c: Coincident(g4,g5)
    c: Coincident(g5,g6)
    c: Coincident(g6,g7)
    c: Coincident(g7,g4)
    c: Horizontal(g4)
    c: Horizontal(g6)
    c: Vertical(g5)
    c: Vertical(g7)
    c: Coincident(g8,g9)
    c: Coincident(g9,g10)
    c: Coincident(g10,g11)
    c: Coincident(g11,g8)
    c: Horizontal(g8)
    c: Horizontal(g10)
    c: Vertical(g9)
    c: Vertical(g11)
    c: Coincident(g12,g2)
    c: Coincident(g12,g4)
    c: Coincident(g13,g6)
    c: Coincident(g13,g8)
    c: Coincident(g14,g1)
    c: Coincident(g14,g4)
    c: Vertical(g14)
    c: Coincident(g15,g5)
    c: Coincident(g15,g8)
    c: Vertical(g12)
    c: Vertical(g13)
    c: Vertical(g15)
    c: Coincident(g16,g-1)
    c: PointOnObject(g16,g-2)
    c: Symmetric(g0,g0,g16)
    c: DistanceX(g10,g9) = 12.25
    c: Equal(g7,g3)
    c: Distance(g1) = 1.5
    c: Distance(g9) = 2
    c: DistanceY(g0,g-1) = 7.75
    c: DistanceY(g4,g-1) = 10.75
    c: DistanceY(g8,g-1) = 15.75
FEATURE [Sketcher::SketchObject] Sketch028
  FullyConstrained = true
  MapMode = 5
  Placement = pos=(0,0,0) rot=(0.57735,0.57735,0.57735;2.0944rad)
  Support = -> [YZ_Plane009]
  sketch-geometry (5):
    g0: LineSegment StartX=-13 StartY=11.5 StartZ=0 EndX=-8 EndY=11.5 EndZ=0
    g1: LineSegment StartX=-13 StartY=11.5 StartZ=0 EndX=-12.4982 EndY=17.4701 EndZ=0
    g2: LineSegment StartX=-11.567 StartY=17.6782 StartZ=0 EndX=-8 EndY=11.5 EndZ=0
    g3: LineSegment StartX=-12 StartY=17.4282 StartZ=0 EndX=-12 EndY=11.5 EndZ=0
    g4: ArcOfCircle CenterX=-12 CenterY=17.4282 CenterZ=0 NormalX=0 NormalY=0 NormalZ=1 AngleXU=0 Radius=0.5 StartAngle=0.523599 EndAngle=3.05774
  constraints (14):
    c: Horizontal(g0)
    c: Coincident(g1,g0)
    c: Coincident(g2,g0)
    c: Angle(g2,g0) = 1.0472
    c: PointOnObject(g3,g0)
    c: Vertical(g3)
    c: DistanceX(g0,g3) = 1
    c: Tangent(g1,g4) = 1.5708
    c: Tangent(g2,g4) = 1.5708
    c: Coincident(g3,g4)
    c: Radius(g4) = 0.5
    c: DistanceY(g-1,g0) = 11.5
    c: DistanceX(g0,g-1) = 8
    c: DistanceX(g3,g0) = 4
FEATURE [PartDesign::Pad] Pad015  label="MainCSExt"
  Direction = (1,1,1)
  Length = 17.3
  Length2 = 100
  Placement = pos=(0,0,0) rot=(1,0,0;1.5708rad)
  Profile = -> Sketch024
  Type = 0
FEATURE [PartDesign::Pocket] Pocket009  label="FeetCut"
  BaseFeature = -> Pad015
  Length = 5
  Length2 = 100
  Midplane = true
  Placement = pos=(0,0,0) rot=(1,0,0;1.5708rad)
  Profile = -> Sketch023
  Type = 1
FEATURE [PartDesign::Pocket] Pocket007  label="BoltHoles"
  BaseFeature = -> Pocket009
  Length = 5
  Length2 = 100
  Midplane = true
  Placement = pos=(0,0,0) rot=(1,0,0;1.5708rad)
  Profile = -> Sketch022
  Type = 1
FEATURE [PartDesign::Pocket] Pocket008  label="HexSunk"
  BaseFeature = -> Pocket007
  Length = 2
  Length2 = 1
  Placement = pos=(0,0,0) rot=(1,0,0;1.5708rad)
  Profile = -> Sketch025
  Type = 4
FEATURE [PartDesign::Pocket] Pocket006  label="BoltHoleClearanceCut"
  BaseFeature = -> Pocket008
  Length = 4
  Length2 = 100
  Placement = pos=(0,0,0) rot=(1,0,0;1.5708rad)
  Profile = -> Sketch026
  Reversed = true
  Type = 0
FEATURE [PartDesign::Pocket] Pocket010  label="MotorPlate Slots"
  BaseFeature = -> Pocket006
  Length = 10
  Length2 = 100
  Placement = pos=(0,0,0) rot=(1,0,0;1.5708rad)
  Profile = -> Sketch027
  Reversed = true
  Type = 0
FEATURE [PartDesign::Pad] Pad016  label="WireGuide"
  BaseFeature = -> Pocket010
  Direction = (1,1,1)
  Length = 13
  Length2 = 100
  Midplane = true
  Placement = pos=(0,0,0) rot=(1,0,0;1.5708rad)
  Profile = -> Sketch028
  Type = 0
FEATURE [PartDesign::Body] Body007  label="PB3D_MotorBracket"
  Group = -> [Sketch024,Pad015,Sketch023,Pocket009,Sketch022,Pocket007,DatumPlane005,Sketch025,Pocket008,Sketch026,Pocket006,Sketch027,Pocket010,Sketch028,Pad016]
  Origin = -> Origin009
  Tip = -> Pad016
FEATURE [App::Part] Part001  label="PB3D_MotorBracketPart"
  Group = -> [Body007]
  Origin = -> Origin008
  Placement = pos=(0,-6,-5) rot=(0,0,1;0rad)
FEATURE [Mesh::Feature] Mesh  label="PB3D_MotorBracket (Meshed)"
